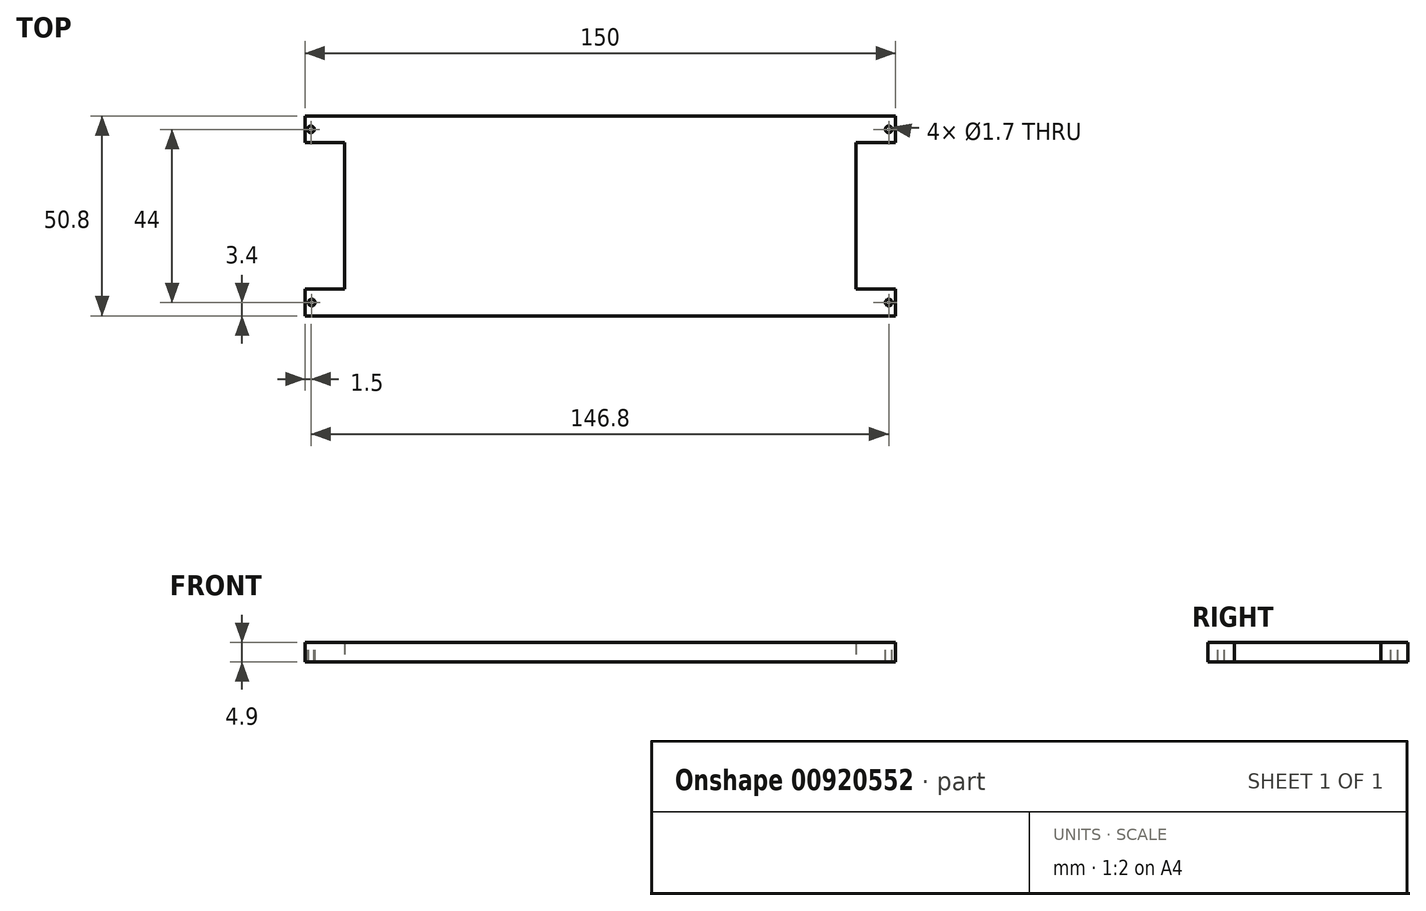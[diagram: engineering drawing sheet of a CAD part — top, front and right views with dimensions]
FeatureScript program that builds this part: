
annotation { "Feature Type Name" : "Feature", "Feature Type Description" : "" }
export const myFeature = defineFeature(function(context is Context, id is Id, definition is map)
    precondition{}
    {
        {
            var Q0;
            Q0=qCreatedBy(makeId("Top.planeOp"),FACE);
            var sketch = newSketch(context, id + "F0", { "sketchPlane" : qUnion([Q0])});
            skLineSegment(sketch, "E0.bottom", {"start": v(75, -25.4) * mm, "end": v(-75, -25.4) * mm});
            skLineSegment(sketch, "E0.top", {"start": v(75, 25.4) * mm, "end": v(-75, 25.4) * mm});
            skLineSegment(sketch, "E0.left", {"start": v(75, -25.4) * mm, "end": v(75, 25.4) * mm});
            skLineSegment(sketch, "E0.right", {"start": v(-75, -25.4) * mm, "end": v(-75, 25.4) * mm});
            skPoint(sketch, "E0.middle", {"position": v(0, 0) * mm});
            skPoint(sketch, "E1", {"position": v(-65, 18.6) * mm});
            skPoint(sketch, "E2", {"position": v(-65, -18.6) * mm});
            skPoint(sketch, "E3", {"position": v(65, -18.6) * mm});
            skPoint(sketch, "E4", {"position": v(65, 18.6) * mm});
            skLineSegment(sketch, "E5", {"start": v(-75, 18.6) * mm, "end": v(-65, 18.6) * mm});
            skLineSegment(sketch, "E6", {"start": v(-65, -18.6) * mm, "end": v(-75, -18.6) * mm});
            skLineSegment(sketch, "E7", {"start": v(-75, -18.6) * mm, "end": v(-65, -18.6) * mm});
            skLineSegment(sketch, "E8", {"start": v(-65, 18.6) * mm, "end": v(-65, -18.6) * mm});
            skLineSegment(sketch, "E9", {"start": v(65, 18.6) * mm, "end": v(65, -18.6) * mm});
            skLineSegment(sketch, "E10", {"start": v(65, -18.6) * mm, "end": v(75, -18.6) * mm});
            skLineSegment(sketch, "E11", {"start": v(65, 18.6) * mm, "end": v(75, 18.6) * mm});
            skSolve(sketch);
        }
        {
            var Q0;
            {var subQ4=sQuery(id+"F0.wireOp",EDGE,"E0.bottom");Q0=makeQuery(id+"F0.imprint","IMPRINT",FACE,{"disambiguationData":[TD([[makeQuery(id+"F0.imprint","IMPRINT",EDGE,{"derivedFrom":subQ4}),-1.0]])]});}
            extrude(context, id + "F1", {"entities" : qUnion([Q0]), "depth" : 4.9 * mm, "offsetDistance" : 25 * mm});
        }
        {
            var Q0;
            Q0=makeQuery(id+"F1.opExtrude","CAP_FACE",FACE,{"disambiguationData":[OSD([sQuery(id+"F0.wireOp",EDGE,"E0.bottom"),sQuery(id+"F0.wireOp",EDGE,"E0.top"),sQuery(id+"F0.wireOp",EDGE,"E0.left"),sQuery(id+"F0.wireOp",EDGE,"E0.right"),sQuery(id+"F0.wireOp",EDGE,"E5"),sQuery(id+"F0.wireOp",EDGE,"E7"),sQuery(id+"F0.wireOp",EDGE,"E8"),sQuery(id+"F0.wireOp",EDGE,"E9"),sQuery(id+"F0.wireOp",EDGE,"E10"),sQuery(id+"F0.wireOp",EDGE,"E11")])],"isStart":false});
            var sketch = newSketch(context, id + "F2", { "sketchPlane" : qUnion([Q0])});
            skPoint(sketch, "E12", {"position": v(-73.5, 22) * mm});
            skPoint(sketch, "E13", {"position": v(-73.3, -22) * mm});
            skPoint(sketch, "E14", {"position": v(73.3, 22) * mm});
            skPoint(sketch, "E15", {"position": v(73.3, -22) * mm});
            skCircle(sketch, "E16", {"center": v(-73.5, 22) * mm, "radius": 0.85 * mm});
            skCircle(sketch, "E17", {"center": v(-73.3, -22) * mm, "radius": 0.85 * mm});
            skCircle(sketch, "E18", {"center": v(73.3, 22) * mm, "radius": 0.85 * mm});
            skCircle(sketch, "E19", {"center": v(73.3, -22) * mm, "radius": 0.85 * mm});
            skSolve(sketch);
        }
        {
            var Q0;
            Q0=makeQuery(id+"F2.imprint","IMPRINT",FACE,{"disambiguationData":[TD([[makeQuery(id+"F2.imprint","IMPRINT",EDGE,{"derivedFrom":sQuery(id+"F2.wireOp",EDGE,"E16")}),1.0]])]});
            var Q1;
            Q1=makeQuery(id+"F2.imprint","IMPRINT",FACE,{"disambiguationData":[TD([[makeQuery(id+"F2.imprint","IMPRINT",EDGE,{"derivedFrom":sQuery(id+"F2.wireOp",EDGE,"E17")}),1.0]])]});
            var Q2;
            Q2=makeQuery(id+"F2.imprint","IMPRINT",FACE,{"disambiguationData":[TD([[makeQuery(id+"F2.imprint","IMPRINT",EDGE,{"derivedFrom":sQuery(id+"F2.wireOp",EDGE,"E18")}),1.0]])]});
            var Q3;
            Q3=makeQuery(id+"F2.imprint","IMPRINT",FACE,{"disambiguationData":[TD([[makeQuery(id+"F2.imprint","IMPRINT",EDGE,{"derivedFrom":sQuery(id+"F2.wireOp",EDGE,"E19")}),1.0]])]});
            extrude(context, id + "F3", {"entities" : qUnion([Q0, Q1, Q2, Q3]), "operationType" : NewBodyOperationType.REMOVE, "endBound" : BoundingType.THROUGH_ALL, "oppositeDirection" : true, "depth" : 25 * mm, "offsetDistance" : 25 * mm});
        }
    });
